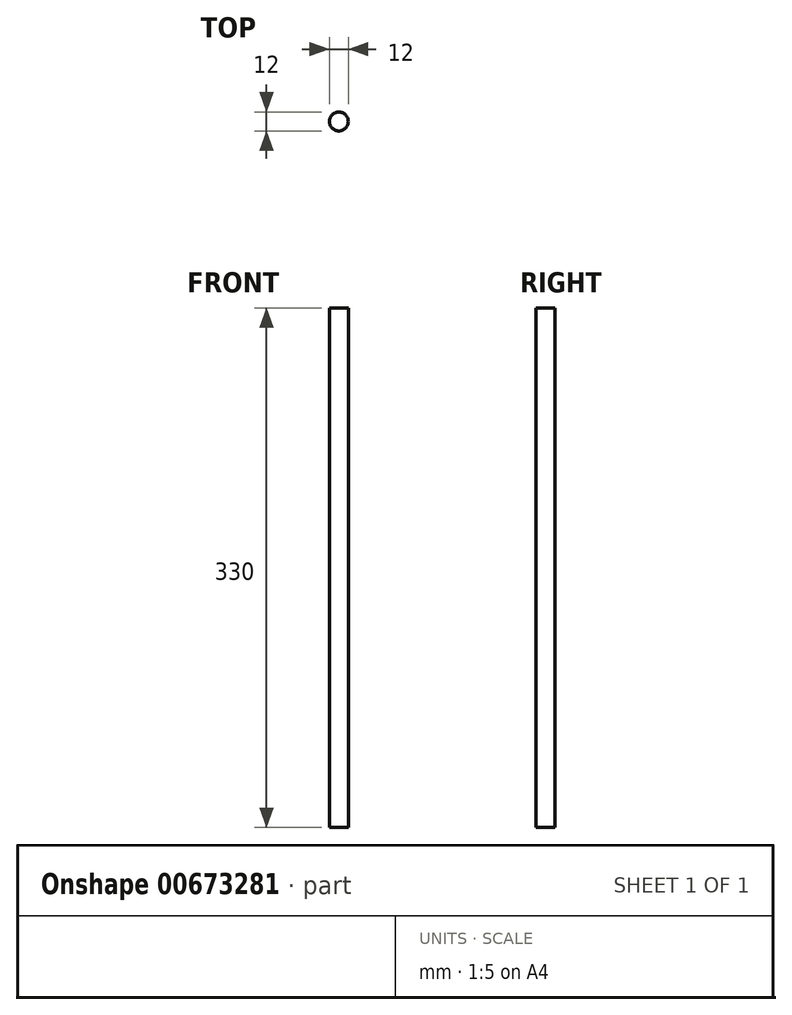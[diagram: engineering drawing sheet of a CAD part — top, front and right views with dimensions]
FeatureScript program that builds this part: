
annotation { "Feature Type Name" : "Feature", "Feature Type Description" : "" }
export const myFeature = defineFeature(function(context is Context, id is Id, definition is map)
    precondition{}
    {
        {
            var Q0;
            Q0=qCreatedBy(makeId("Top.planeOp"),FACE);
            var sketch = newSketch(context, id + "F0", { "sketchPlane" : qUnion([Q0])});
            skCircle(sketch, "E0", {"center": v(0, 0) * mm, "radius": 6 * mm});
            skSolve(sketch);
        }
        {
            var Q0;
            Q0=qSketchRegion(id+"F0",true);
            extrude(context, id + "F1", {"entities" : qUnion([Q0]), "depth" : 330 * mm, "offsetDistance" : 25 * mm});
        }
    });
